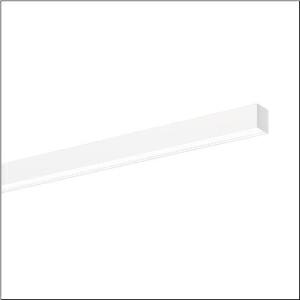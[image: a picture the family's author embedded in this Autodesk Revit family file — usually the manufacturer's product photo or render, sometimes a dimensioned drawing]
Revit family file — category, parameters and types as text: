
# Revit family: silica_r__21_51mx23db45wb_81de
name_source: partatom
category: Lighting Fixtures
units: mm (PartAtom-declared; Revit-internal decimal feet)

## family parameters
Cut with Voids When Loaded = No
Host = Face
Light Source = No
Part Type = Normal
Room Calculation Point = No
Round Connector Dimension = Use Diameter
Shared = No

## types (1)
- --- (1 x LED, 4100 lm, 28.1 W, 4000K)
    Apparent Load = 28 VA
    CIE Flux Codes = 78 96 99 100 100
    Color Rendering = 80
    Color Temperature = 4000K
    Default Elevation = 1800 mm
    Description = Silica® 21, office luminaire, primary optical cover: prismatic diffuser, of PMMA, CAT 2 (L<= 3000cd/m²), light emission: direct distribution, primary light characteristic: symmetric, installation type: surface-mounted, LED, rated luminous flux: 4.100lm, luminous efficacy: 146lm/W, light colour: 840, colour temperature: 4000K, with terminal, 3+2-pole, max. 2.5mm², mains connection: 220..240V, AC, 50/60Hz, rated input power: 28.1W, luminaire housing, of aluminium, traffic white (RAL 9016), length: 1.504mm, width: 53mm, height: 53mm, protection rating (complete): IP20, insulation class (complete): insulation class I (protective earthing), certification: CE, permissible operating ambient temperature: 0..+35°C, standard: EN 50419, packaging unit: 1 piece
    Height = 0 mm  [stored 0 ft]
    Lamp = 1 x LED
    Lamp Light Flux = 4100 lm
    Lamp Power = 28.1 W
    Lamp count = 1
    Length = 1504 mm
    Luminous efficacy = 146 lm/W
    Manufacturer = Siteco
    ModVariant = No
    Model = 51MX23DB45WB
    Mounting Place = Ceiling
    Mounting Type = Recessed
    Number of Poles = 1
    OnlyDefault = Yes
    Power Factor = 1
    Product Name = Silica® 21
    Product group = office luminaire | ceiling recessed
    ProductGroupID = 401
    Protection Class = Protection class I
    Protection Degree = IP 20
    RLX_Detail_Level = 1
    RLX_Emergency_Light_Flux = 0 lm
    RLX_Emergency_Type = 0
    RLX_Emergency_Type_DB = No
    RlxData = <blob elided: 18893 chars, md5=858b4148>
    Socket = socket
    Standby Power = 0 W
    System Light Flux = 4100 lm
    System Power = 28 W
    Type Comments = factory setting: luminous flux: 100 % | dim-lin: 254 | 323 mA
    Type Image = l_1297777.jpg
    URL = http://relux.com
    VarID = @adj_050201
    Voltage = 0 V
    Weight = 0.00 kg
    Width = 53 mm

note: [stored X ft] marks values corroborated as IEEE doubles in the binary element streams (Revit-internal decimal feet)

## geometry (parser evidence)
native form markers: Blend x4, Sweep x14
no freeform markers — native parametric forms only
